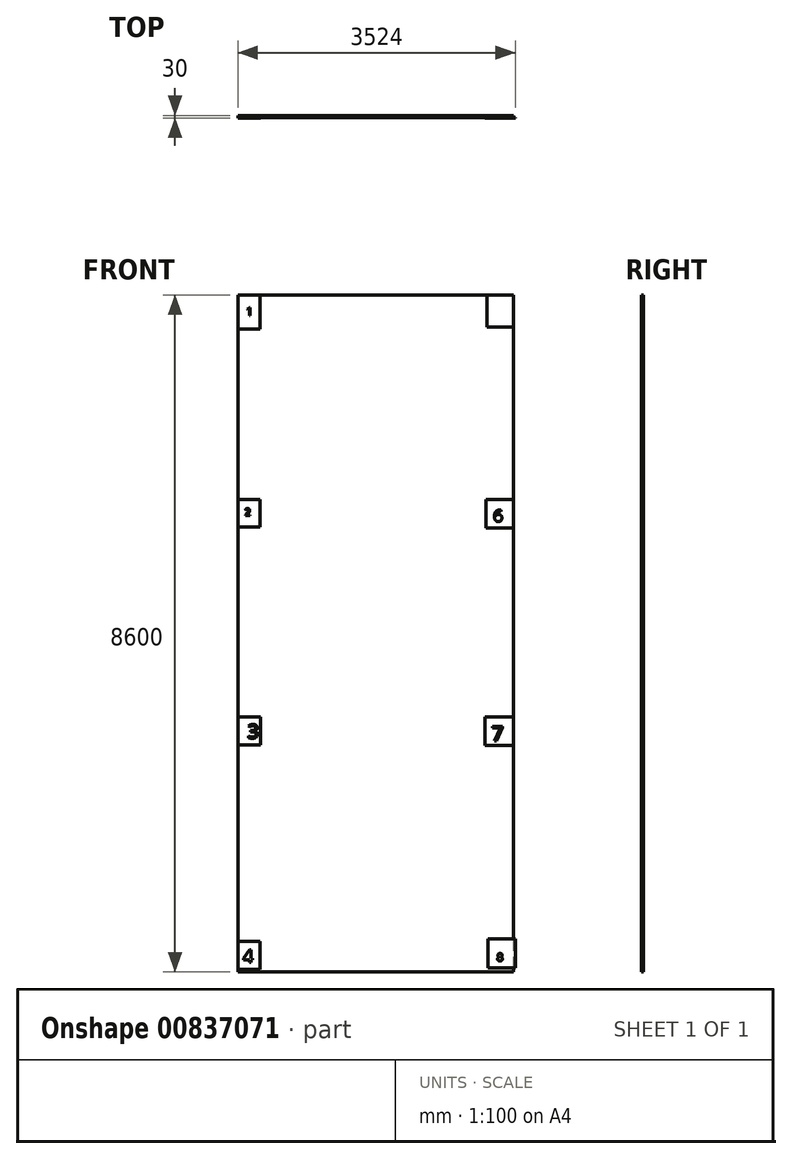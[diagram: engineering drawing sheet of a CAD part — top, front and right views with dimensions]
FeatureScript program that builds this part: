
annotation { "Feature Type Name" : "Feature", "Feature Type Description" : "" }
export const myFeature = defineFeature(function(context is Context, id is Id, definition is map)
    precondition{}
    {
        {
            var Q0;
            Q0=qCreatedBy(makeId("Front.planeOp"),FACE);
            var sketch = newSketch(context, id + "F0", { "sketchPlane" : qUnion([Q0])});
            skLineSegment(sketch, "E0.bottom", {"start": v(-1770.31, 7429.9) * mm, "end": v(1729.69, 7429.9) * mm});
            skLineSegment(sketch, "E0.top", {"start": v(-1770.31, -1170.1) * mm, "end": v(1729.69, -1170.1) * mm});
            skLineSegment(sketch, "E0.left", {"start": v(-1770.31, 7429.9) * mm, "end": v(-1770.31, -1170.1) * mm});
            skLineSegment(sketch, "E0.right", {"start": v(1729.69, 7429.9) * mm, "end": v(1729.69, -1170.1) * mm});
            skSolve(sketch);
        }
        {
            var Q0;
            Q0 = qSketchRegion(id + "F0", true);
            extrude(context, id + "F1", {"entities" : qUnion([Q0]), "depth" : 25 * mm, "offsetDistance" : 25 * mm});
        }
        {
            var Q0;
            Q0=makeQuery(id+"F1.opExtrude","CAP_FACE",FACE,{"disambiguationData":[OSD([sQuery(id+"F0.wireOp",EDGE,"E0.bottom"),sQuery(id+"F0.wireOp",EDGE,"E0.top"),sQuery(id+"F0.wireOp",EDGE,"E0.left"),sQuery(id+"F0.wireOp",EDGE,"E0.right")])],"isStart":false});
            var sketch = newSketch(context, id + "F2", { "sketchPlane" : qUnion([Q0])});
            skLineSegment(sketch, "E1.bottom", {"start": v(-1770.31, 7429.9) * mm, "end": v(-1490.31, 7429.9) * mm});
            skLineSegment(sketch, "E1.top", {"start": v(-1770.31, 6999.9) * mm, "end": v(-1490.31, 6999.9) * mm});
            skLineSegment(sketch, "E1.left", {"start": v(-1770.31, 7429.9) * mm, "end": v(-1770.31, 6999.9) * mm});
            skLineSegment(sketch, "E1.right", {"start": v(-1490.31, 7429.9) * mm, "end": v(-1490.31, 6999.9) * mm});
            skLineSegment(sketch, "E2.bottom", {"start": v(-1770.31, 4829.9) * mm, "end": v(-1490.31, 4829.9) * mm});
            skLineSegment(sketch, "E2.top", {"start": v(-1770.31, 4479.9) * mm, "end": v(-1490.31, 4479.9) * mm});
            skLineSegment(sketch, "E2.left", {"start": v(-1770.31, 4829.9) * mm, "end": v(-1770.31, 4479.9) * mm});
            skLineSegment(sketch, "E2.right", {"start": v(-1490.31, 4829.9) * mm, "end": v(-1490.31, 4479.9) * mm});
            skLineSegment(sketch, "E3.bottom", {"start": v(-1770.31, 2069.9) * mm, "end": v(-1480.31, 2069.9) * mm});
            skLineSegment(sketch, "E3.top", {"start": v(-1770.31, 1714.9) * mm, "end": v(-1480.31, 1714.9) * mm});
            skLineSegment(sketch, "E3.left", {"start": v(-1770.31, 2069.9) * mm, "end": v(-1770.31, 1714.9) * mm});
            skLineSegment(sketch, "E3.right", {"start": v(-1480.31, 2069.9) * mm, "end": v(-1480.31, 1714.9) * mm});
            skLineSegment(sketch, "E4.bottom", {"start": v(-1770.31, -780.1) * mm, "end": v(-1490.31, -780.1) * mm});
            skLineSegment(sketch, "E4.top", {"start": v(-1770.31, -1135.1) * mm, "end": v(-1490.31, -1135.1) * mm});
            skLineSegment(sketch, "E4.left", {"start": v(-1770.31, -780.1) * mm, "end": v(-1770.31, -1135.1) * mm});
            skLineSegment(sketch, "E4.right", {"start": v(-1490.31, -780.1) * mm, "end": v(-1490.31, -1135.1) * mm});
            skLineSegment(sketch, "E5.bottom", {"start": v(1729.69, 7429.9) * mm, "end": v(1394.69, 7429.9) * mm});
            skLineSegment(sketch, "E5.top", {"start": v(1754.69, 7019.9) * mm, "end": v(1394.69, 7019.9) * mm});
            skLineSegment(sketch, "E5.left", {"start": v(1754.69, 7429.9) * mm, "end": v(1754.69, 7019.9) * mm});
            skLineSegment(sketch, "E5.right", {"start": v(1394.69, 7429.9) * mm, "end": v(1394.69, 7019.9) * mm});
            skLineSegment(sketch, "E6.bottom", {"start": v(1379.69, 4829.9) * mm, "end": v(1729.69, 4829.9) * mm});
            skLineSegment(sketch, "E6.top", {"start": v(1379.69, 4469.9) * mm, "end": v(1729.69, 4469.9) * mm});
            skLineSegment(sketch, "E6.left", {"start": v(1379.69, 4829.9) * mm, "end": v(1379.69, 4469.9) * mm});
            skLineSegment(sketch, "E6.right", {"start": v(1729.69, 4829.9) * mm, "end": v(1729.69, 4469.9) * mm});
            skLineSegment(sketch, "E7.bottom", {"start": v(1369.69, 2069.9) * mm, "end": v(1729.69, 2069.9) * mm});
            skLineSegment(sketch, "E7.top", {"start": v(1369.69, 1709.9) * mm, "end": v(1729.69, 1709.9) * mm});
            skLineSegment(sketch, "E7.left", {"start": v(1369.69, 2069.9) * mm, "end": v(1369.69, 1709.9) * mm});
            skLineSegment(sketch, "E7.right", {"start": v(1729.69, 2069.9) * mm, "end": v(1729.69, 1709.9) * mm});
            skLineSegment(sketch, "E8.bottom", {"start": v(1408.69, -750.1) * mm, "end": v(1753.69, -750.1) * mm});
            skLineSegment(sketch, "E8.top", {"start": v(1408.69, -1120.1) * mm, "end": v(1753.69, -1120.1) * mm});
            skLineSegment(sketch, "E8.left", {"start": v(1408.69, -750.1) * mm, "end": v(1408.69, -1120.1) * mm});
            skLineSegment(sketch, "E8.right", {"start": v(1753.69, -750.1) * mm, "end": v(1753.69, -1120.1) * mm});
            skText(sketch, "E9", { "text": "1", "fontName": "OpenSans-Regular.ttf"});
            skText(sketch, "E10", { "text": "2", "fontName": "OpenSans-Regular.ttf"});
            skText(sketch, "E11", { "text": "3", "fontName": "OpenSans-Regular.ttf"});
            skText(sketch, "E12", { "text": "4", "fontName": "OpenSans-Regular.ttf"});
            skText(sketch, "E13", { "text": "5", "fontName": "OpenSans-Regular.ttf"});
            skText(sketch, "E14", { "text": "7", "fontName": "OpenSans-Regular.ttf"});
            skText(sketch, "E15", { "text": "8", "fontName": "OpenSans-Regular.ttf"});
            skPoint(sketch, "E15.firstSnap0", {"position": v(1408.69, -935.1) * mm});
            skText(sketch, "E16", { "text": "6", "fontName": "OpenSans-Regular.ttf"});
            const initialGuessF2  = {"E9": [-1.66392, 7.16808, 1, 0, 0.10348], "E10": [-1.68208, 4.62664, 1, 0, 0.09016], "E11": [-1.64612, 1.80018, 1, 0, 0.17458], "E12": [-1.70553, -1.04936, 1, 0, 0.15894], "E13": [1.49154, 7.09082, 1, 0, 0.17629], "E14": [1.45114, 1.76486, 1, 0, 0.18883], "E15": [1.5215, -1.02863, 1, 0, 0.09354], "E16": [1.4766, 4.55237, 1, 0, 0.1453]};
            skSetInitialGuess(sketch, initialGuessF2);
            skSolve(sketch);
        }
        {
            var Q0;
            Q0 = qSketchRegion(id + "F2", true);
            var Q1;
            {var subQ0=sQuery(id+"F2.wireOp",EDGE,"E5.bottom");Q1=makeQuery(id+"F2.imprint","IMPRINT",FACE,{"disambiguationData":[TD([[makeQuery(id+"F2.imprint","IMPRINT",EDGE,{"derivedFrom":subQ0}),-1.0]])]});}
            extrude(context, id + "F3", {"entities" : qUnion([Q0, Q1]), "operationType" : NewBodyOperationType.ADD, "depth" : 5 * mm, "offsetDistance" : 25 * mm});
        }
    });
